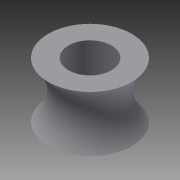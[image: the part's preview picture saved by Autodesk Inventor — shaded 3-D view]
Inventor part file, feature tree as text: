
AUTODESK INVENTOR PART (.ipt)
format: ipt  version: 2015 (Build 190159000, 159)  size: 139,776 bytes
history: native  units: in
note: dims shown in document units (in); Inventor stores cm internally (conversion verified against a paired STEP export)
features: sketch x3, extrude x2, revolve x1
ambient origin geometry x8: Origin, YZ Plane, XZ Plane, XY Plane, X Axis, Y Axis, Z Axis, Center Point
bodies: Solid1 (feature_tree)
feature tree (6):
  revolve  "Revolution1"  [1 undecoded]
  extrude  "Extrusion1"  Depth=0.3in
  extrude  "Extrusion2"  Depth=0.0551in
  sketch  "Sketch1"  dims[d0=90.0deg d1=0.4in]
  sketch  "Sketch2"  dims[d2=0.3in d3=0.4331in]
  sketch  "Sketch3"  dims[d4=0.0551in d5=0.0in d6=0.3091in d7=0.0551in d8=0.0in]
note: 1 required parameter value undecoded (feature->parameter linkage not recoverable at this tier; creation-order binding heuristic only, values carry confidence <= 0.55)
